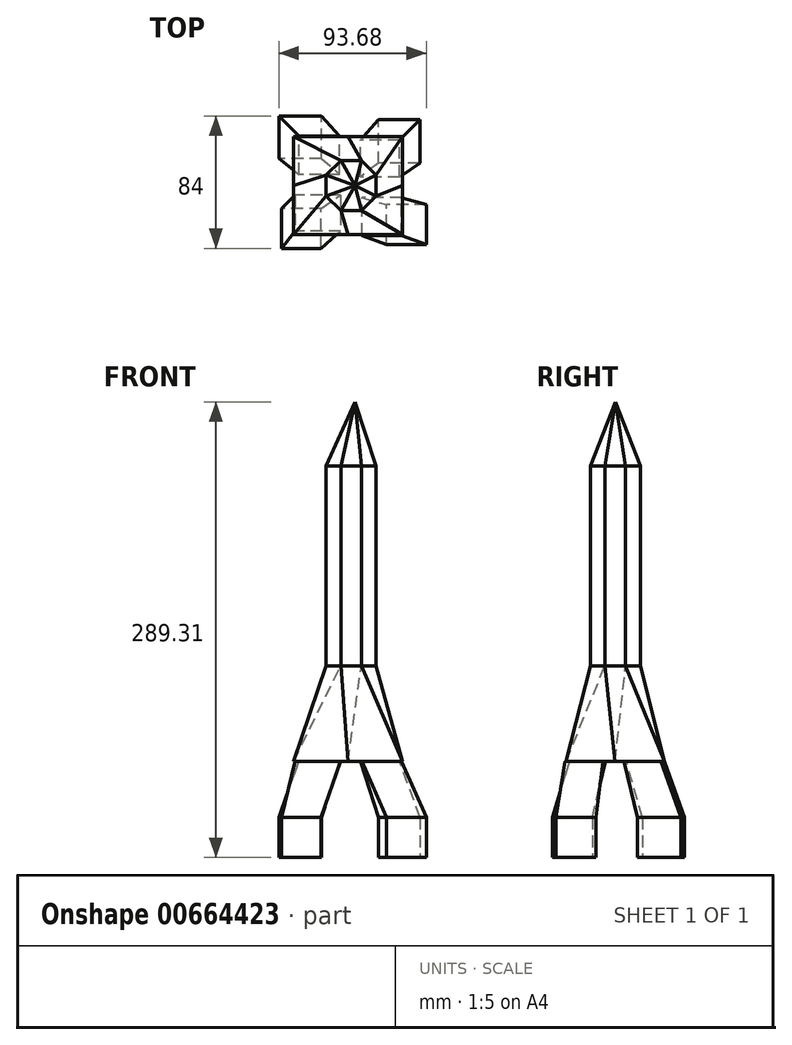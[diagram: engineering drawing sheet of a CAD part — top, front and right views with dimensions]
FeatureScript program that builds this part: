
annotation { "Feature Type Name" : "Feature", "Feature Type Description" : "" }
export const myFeature = defineFeature(function(context is Context, id is Id, definition is map)
    precondition{}
    {
        {
            var Q0;
            Q0=qCreatedBy(makeId("Top.planeOp"),FACE);
            var sketch = newSketch(context, id + "F0", { "sketchPlane" : qUnion([Q0])});
            skLineSegment(sketch, "E0.bottom", {"start": v(48.34, -37.68) * mm, "end": v(22.94, -37.68) * mm});
            skLineSegment(sketch, "E0.top", {"start": v(48.34, -12.28) * mm, "end": v(22.94, -12.28) * mm});
            skLineSegment(sketch, "E0.left", {"start": v(48.34, -37.68) * mm, "end": v(48.34, -12.28) * mm});
            skLineSegment(sketch, "E0.right", {"start": v(22.94, -37.68) * mm, "end": v(22.94, -12.28) * mm});
            skLineSegment(sketch, "E1.bottom", {"start": v(-18.47, -40.03) * mm, "end": v(-43.61, -40.03) * mm});
            skLineSegment(sketch, "E1.top", {"start": v(-18.47, -14.63) * mm, "end": v(-43.61, -14.63) * mm});
            skLineSegment(sketch, "E1.left", {"start": v(-18.47, -40.03) * mm, "end": v(-18.47, -14.63) * mm});
            skLineSegment(sketch, "E1.right", {"start": v(-43.61, -40.03) * mm, "end": v(-43.61, -14.63) * mm});
            skLineSegment(sketch, "E2.bottom", {"start": v(44.34, 14.1) * mm, "end": v(18.05, 14.1) * mm});
            skLineSegment(sketch, "E2.top", {"start": v(44.34, 41.53) * mm, "end": v(18.05, 41.53) * mm});
            skLineSegment(sketch, "E2.left", {"start": v(44.34, 14.1) * mm, "end": v(44.34, 41.53) * mm});
            skLineSegment(sketch, "E2.right", {"start": v(18.05, 14.1) * mm, "end": v(18.05, 41.53) * mm});
            skLineSegment(sketch, "E3.bottom", {"start": v(-18.32, 17.15) * mm, "end": v(-45.34, 17.15) * mm});
            skLineSegment(sketch, "E3.top", {"start": v(-18.32, 43.97) * mm, "end": v(-45.34, 43.97) * mm});
            skLineSegment(sketch, "E3.left", {"start": v(-18.32, 17.15) * mm, "end": v(-18.32, 43.97) * mm});
            skLineSegment(sketch, "E3.right", {"start": v(-45.34, 17.15) * mm, "end": v(-45.34, 43.97) * mm});
            skSolve(sketch);
        }
        {
            var Q0;
            Q0=makeQuery(id+"F0.imprint","IMPRINT",FACE,{"disambiguationData":[TD([[makeQuery(id+"F0.imprint","IMPRINT",EDGE,{"derivedFrom":sQuery(id+"F0.wireOp",EDGE,"E0.bottom")}),-1.0]])]});
            var Q1;
            Q1=makeQuery(id+"F0.imprint","IMPRINT",FACE,{"disambiguationData":[TD([[makeQuery(id+"F0.imprint","IMPRINT",EDGE,{"derivedFrom":sQuery(id+"F0.wireOp",EDGE,"E2.bottom")}),-1.0]])]});
            var Q2;
            Q2=makeQuery(id+"F0.imprint","IMPRINT",FACE,{"disambiguationData":[TD([[makeQuery(id+"F0.imprint","IMPRINT",EDGE,{"derivedFrom":sQuery(id+"F0.wireOp",EDGE,"E3.bottom")}),-1.0]])]});
            var Q3;
            Q3=makeQuery(id+"F0.imprint","IMPRINT",FACE,{"disambiguationData":[TD([[makeQuery(id+"F0.imprint","IMPRINT",EDGE,{"derivedFrom":sQuery(id+"F0.wireOp",EDGE,"E1.bottom")}),-1.0]])]});
            extrude(context, id + "F1", {"entities" : qUnion([Q0, Q1, Q2, Q3]), "depth" : 25.4 * mm, "offsetDistance" : 25.4 * mm});
        }
        {
            var Q0;
            Q0=makeQuery(id+"F1.opExtrude","CAP_FACE",FACE,{"disambiguationData":[OSD([sQuery(id+"F0.wireOp",EDGE,"E0.bottom"),sQuery(id+"F0.wireOp",EDGE,"E0.top"),sQuery(id+"F0.wireOp",EDGE,"E0.left"),sQuery(id+"F0.wireOp",EDGE,"E0.right")])],"isStart":false});
            cPlane(context, id + "F2", {"entities" : qUnion([Q0]), "cplaneType" : CPlaneType.OFFSET, "offset" : 35.56 * mm, "width" : 152.4 * mm, "height" : 152.4 * mm});
        }
        {
            var Q0;
            Q0=makeQuery(id+"F1.opExtrude","CAP_FACE",FACE,{"disambiguationData":[OSD([sQuery(id+"F0.wireOp",EDGE,"E3.bottom"),sQuery(id+"F0.wireOp",EDGE,"E3.top"),sQuery(id+"F0.wireOp",EDGE,"E3.left"),sQuery(id+"F0.wireOp",EDGE,"E3.right")])],"isStart":false});
            var sketch = newSketch(context, id + "F3", { "sketchPlane" : qUnion([Q0])});
            skSolve(sketch);
        }
        {
            var Q0;
            Q0=makeQuery(id+"F3.imprint","IMPRINT",FACE,{"disambiguationData":[TD([[makeQuery(id+"F3.imprint","IMPRINT",EDGE,{"derivedFrom":makeQuery(id+"F1.opExtrude","CAP_EDGE",EDGE,{"disambiguationData":[OSD([sQuery(id+"F0.wireOp",EDGE,"E3.bottom")])],"isStart":false})}),-1.0]])]});
            var sketch = newSketch(context, id + "F4", { "sketchPlane" : qUnion([Q0])});
            skLineSegment(sketch, "E4.bottom", {"start": v(-18.27, 43.99) * mm, "end": v(-45.5, 43.99) * mm});
            skLineSegment(sketch, "E4.top", {"start": v(-18.27, 17.13) * mm, "end": v(-45.5, 17.13) * mm});
            skLineSegment(sketch, "E4.left", {"start": v(-18.27, 43.99) * mm, "end": v(-18.27, 17.13) * mm});
            skLineSegment(sketch, "E4.right", {"start": v(-45.5, 43.99) * mm, "end": v(-45.5, 17.13) * mm});
            skLineSegment(sketch, "E5.bottom", {"start": v(44.38, 41.75) * mm, "end": v(18.04, 41.75) * mm});
            skLineSegment(sketch, "E5.top", {"start": v(44.38, 14.12) * mm, "end": v(18.04, 14.12) * mm});
            skLineSegment(sketch, "E5.left", {"start": v(44.38, 41.75) * mm, "end": v(44.38, 14.12) * mm});
            skLineSegment(sketch, "E5.right", {"start": v(18.04, 41.75) * mm, "end": v(18.04, 14.12) * mm});
            skLineSegment(sketch, "E6.bottom", {"start": v(48.26, -12.22) * mm, "end": v(22.94, -12.22) * mm});
            skLineSegment(sketch, "E6.top", {"start": v(48.26, -37.4) * mm, "end": v(22.94, -37.4) * mm});
            skLineSegment(sketch, "E6.left", {"start": v(48.26, -12.22) * mm, "end": v(48.26, -37.4) * mm});
            skLineSegment(sketch, "E6.right", {"start": v(22.94, -12.22) * mm, "end": v(22.94, -37.4) * mm});
            skLineSegment(sketch, "E7.bottom", {"start": v(-18.8, -14.52) * mm, "end": v(-43.7, -14.52) * mm});
            skLineSegment(sketch, "E7.top", {"start": v(-18.8, -39.99) * mm, "end": v(-43.7, -39.99) * mm});
            skLineSegment(sketch, "E7.left", {"start": v(-18.8, -14.52) * mm, "end": v(-18.8, -39.99) * mm});
            skLineSegment(sketch, "E7.right", {"start": v(-43.7, -14.52) * mm, "end": v(-43.7, -39.99) * mm});
            skSolve(sketch);
        }
        {
            var Q0;
            Q0=qCreatedBy(id+"F2.planeOp",FACE);
            var sketch = newSketch(context, id + "F5", { "sketchPlane" : qUnion([Q0])});
            skLineSegment(sketch, "E8.bottom", {"start": v(36.26, 35.18) * mm, "end": v(10.32, 35.18) * mm});
            skLineSegment(sketch, "E8.top", {"start": v(36.26, 8.93) * mm, "end": v(10.32, 8.93) * mm});
            skLineSegment(sketch, "E8.left", {"start": v(36.26, 35.18) * mm, "end": v(36.26, 8.93) * mm});
            skLineSegment(sketch, "E8.right", {"start": v(10.32, 35.18) * mm, "end": v(10.32, 8.93) * mm});
            skLineSegment(sketch, "E9.bottom", {"start": v(-6.68, 34.58) * mm, "end": v(-34.12, 34.58) * mm});
            skLineSegment(sketch, "E9.top", {"start": v(-6.68, 8.93) * mm, "end": v(-34.12, 8.93) * mm});
            skLineSegment(sketch, "E9.left", {"start": v(-6.68, 34.58) * mm, "end": v(-6.68, 8.93) * mm});
            skLineSegment(sketch, "E9.right", {"start": v(-34.12, 34.58) * mm, "end": v(-34.12, 8.93) * mm});
            skLineSegment(sketch, "E10.bottom", {"start": v(-6.09, -6.28) * mm, "end": v(-35.01, -6.28) * mm});
            skLineSegment(sketch, "E10.top", {"start": v(-6.09, -28.94) * mm, "end": v(-35.01, -28.94) * mm});
            skLineSegment(sketch, "E10.left", {"start": v(-6.09, -6.28) * mm, "end": v(-6.09, -28.94) * mm});
            skLineSegment(sketch, "E10.right", {"start": v(-35.01, -6.28) * mm, "end": v(-35.01, -28.94) * mm});
            skLineSegment(sketch, "E11.bottom", {"start": v(37.75, -5.38) * mm, "end": v(11.21, -5.38) * mm});
            skLineSegment(sketch, "E11.top", {"start": v(37.75, -28.94) * mm, "end": v(11.21, -28.94) * mm});
            skLineSegment(sketch, "E11.left", {"start": v(37.75, -5.38) * mm, "end": v(37.75, -28.94) * mm});
            skLineSegment(sketch, "E11.right", {"start": v(11.21, -5.38) * mm, "end": v(11.21, -28.94) * mm});
            skSolve(sketch);
        }
        {
            var Q1;
            Q1=makeQuery(id+"F1.opExtrude","CAP_FACE",FACE,{"disambiguationData":[OSD([sQuery(id+"F0.wireOp",EDGE,"E1.bottom"),sQuery(id+"F0.wireOp",EDGE,"E1.top"),sQuery(id+"F0.wireOp",EDGE,"E1.left"),sQuery(id+"F0.wireOp",EDGE,"E1.right")])],"isStart":false});
            var Q2;
            Q2=makeQuery(id+"F5.imprint","IMPRINT",FACE,{"disambiguationData":[TD([[makeQuery(id+"F5.imprint","IMPRINT",EDGE,{"derivedFrom":sQuery(id+"F5.wireOp",EDGE,"E10.bottom")}),1.0]])]});
            loft(context, id + "F6", {"operationType" : NewBodyOperationType.ADD, "sheetProfilesArray" : [{ "sheetProfileEntities" : qUnion([Q1]) }, { "sheetProfileEntities" : qUnion([Q2]) }]});
        }
        {
            var Q0;
            Q0=qCreatedBy(id+"F2.planeOp",FACE);
            var sketch = newSketch(context, id + "F7", { "sketchPlane" : qUnion([Q0])});
            skLineSegment(sketch, "E12.bottom", {"start": v(-8.35, 7.38) * mm, "end": v(-34.25, 7.38) * mm});
            skLineSegment(sketch, "E12.top", {"start": v(-8.35, 30.2) * mm, "end": v(-34.25, 30.2) * mm});
            skLineSegment(sketch, "E12.left", {"start": v(-8.35, 7.38) * mm, "end": v(-8.35, 30.2) * mm});
            skLineSegment(sketch, "E12.right", {"start": v(-34.25, 7.38) * mm, "end": v(-34.25, 30.2) * mm});
            skLineSegment(sketch, "E13.bottom", {"start": v(31.36, 5.4) * mm, "end": v(6.57, 5.4) * mm});
            skLineSegment(sketch, "E13.top", {"start": v(31.36, 28.89) * mm, "end": v(6.57, 28.89) * mm});
            skLineSegment(sketch, "E13.left", {"start": v(31.36, 5.4) * mm, "end": v(31.36, 28.89) * mm});
            skLineSegment(sketch, "E13.right", {"start": v(6.57, 5.4) * mm, "end": v(6.57, 28.89) * mm});
            skLineSegment(sketch, "E14.bottom", {"start": v(30.48, -29.48) * mm, "end": v(6.35, -29.48) * mm});
            skLineSegment(sketch, "E14.top", {"start": v(30.48, -7.32) * mm, "end": v(6.35, -7.32) * mm});
            skLineSegment(sketch, "E14.left", {"start": v(30.48, -29.48) * mm, "end": v(30.48, -7.32) * mm});
            skLineSegment(sketch, "E14.right", {"start": v(6.35, -29.48) * mm, "end": v(6.35, -7.32) * mm});
            skSolve(sketch);
        }
        {
            var Q1;
            Q1=makeQuery(id+"F4.imprint","IMPRINT",FACE,{"disambiguationData":[TD([[makeQuery(id+"F4.imprint","IMPRINT",EDGE,{"derivedFrom":sQuery(id+"F4.wireOp",EDGE,"E5.bottom")}),1.0]])]});
            var Q2;
            Q2=makeQuery(id+"F7.imprint","IMPRINT",FACE,{"disambiguationData":[TD([[makeQuery(id+"F7.imprint","IMPRINT",EDGE,{"derivedFrom":sQuery(id+"F7.wireOp",EDGE,"E13.bottom")}),-1.0]])]});
            loft(context, id + "F8", {"operationType" : NewBodyOperationType.ADD, "sheetProfilesArray" : [{ "sheetProfileEntities" : qUnion([Q1]) }, { "sheetProfileEntities" : qUnion([Q2]) }]});
        }
        {
            var Q0;
            Q0=qCreatedBy(id+"F2.planeOp",FACE);
            var sketch = newSketch(context, id + "F9", { "sketchPlane" : qUnion([Q0])});
            skLineSegment(sketch, "E15.bottom", {"start": v(32.64, -31.9) * mm, "end": v(7.33, -31.9) * mm});
            skLineSegment(sketch, "E15.top", {"start": v(32.64, -7.9) * mm, "end": v(7.33, -7.9) * mm});
            skLineSegment(sketch, "E15.left", {"start": v(32.64, -31.9) * mm, "end": v(32.64, -7.9) * mm});
            skLineSegment(sketch, "E15.right", {"start": v(7.33, -31.9) * mm, "end": v(7.33, -7.9) * mm});
            skSolve(sketch);
        }
        {
            var Q1;
            Q1=makeQuery(id+"F9.imprint","IMPRINT",FACE,{"disambiguationData":[TD([[makeQuery(id+"F9.imprint","IMPRINT",EDGE,{"derivedFrom":sQuery(id+"F9.wireOp",EDGE,"E15.bottom")}),-1.0]])]});
            var Q2;
            Q2=makeQuery(id+"F1.opExtrude","CAP_FACE",FACE,{"disambiguationData":[OSD([sQuery(id+"F0.wireOp",EDGE,"E0.bottom"),sQuery(id+"F0.wireOp",EDGE,"E0.top"),sQuery(id+"F0.wireOp",EDGE,"E0.left"),sQuery(id+"F0.wireOp",EDGE,"E0.right")])],"isStart":false});
            loft(context, id + "F10", {"operationType" : NewBodyOperationType.ADD, "sheetProfilesArray" : [{ "sheetProfileEntities" : qUnion([Q1]) }, { "sheetProfileEntities" : qUnion([Q2]) }]});
        }
        {
            var Q0;
            Q0=qCreatedBy(id+"F2.planeOp",FACE);
            var sketch = newSketch(context, id + "F11", { "sketchPlane" : qUnion([Q0])});
            skLineSegment(sketch, "E16.bottom", {"start": v(-6.76, 6.98) * mm, "end": v(-32.6, 6.98) * mm});
            skLineSegment(sketch, "E16.top", {"start": v(-6.76, 31.25) * mm, "end": v(-32.6, 31.25) * mm});
            skLineSegment(sketch, "E16.left", {"start": v(-6.76, 6.98) * mm, "end": v(-6.76, 31.25) * mm});
            skLineSegment(sketch, "E16.right", {"start": v(-32.6, 6.98) * mm, "end": v(-32.6, 31.25) * mm});
            skSolve(sketch);
        }
        {
            var Q1;
            Q1=makeQuery(id+"F3.imprint","IMPRINT",FACE,{"disambiguationData":[TD([[makeQuery(id+"F3.imprint","IMPRINT",EDGE,{"derivedFrom":makeQuery(id+"F1.opExtrude","CAP_EDGE",EDGE,{"disambiguationData":[OSD([sQuery(id+"F0.wireOp",EDGE,"E3.bottom")])],"isStart":false})}),-1.0]])]});
            var Q2;
            Q2=makeQuery(id+"F11.imprint","IMPRINT",FACE,{"disambiguationData":[TD([[makeQuery(id+"F11.imprint","IMPRINT",EDGE,{"derivedFrom":sQuery(id+"F11.wireOp",EDGE,"E16.bottom")}),-1.0]])]});
            loft(context, id + "F12", {"operationType" : NewBodyOperationType.ADD, "sheetProfilesArray" : [{ "sheetProfileEntities" : qUnion([Q1]) }, { "sheetProfileEntities" : qUnion([Q2]) }]});
        }
        {
            var Q0;
            Q0=qCreatedBy(id+"F2.planeOp",FACE);
            cPlane(context, id + "F13", {"entities" : qUnion([Q0]), "cplaneType" : CPlaneType.OFFSET, "offset" : 60.7 * mm, "width" : 152.4 * mm, "height" : 152.4 * mm});
        }
        {
            var Q0;
            Q0=qCreatedBy(id+"F13.planeOp",FACE);
            var sketch = newSketch(context, id + "F14", { "sketchPlane" : qUnion([Q0])});
            skCircle(sketch, "E17.cCircle", {"center": v(0.55, -0.07) * mm, "radius": 15.87 * mm, "construction": true});
            skLineSegment(sketch, "E17.0", {"start": v(-15.32, -6.65) * mm, "end": v(-15.32, 6.5) * mm});
            skLineSegment(sketch, "E17.1", {"start": v(-15.32, 6.5) * mm, "end": v(-6.02, 15.8) * mm});
            skLineSegment(sketch, "E17.2", {"start": v(-6.02, 15.8) * mm, "end": v(7.13, 15.8) * mm});
            skLineSegment(sketch, "E17.3", {"start": v(7.13, 15.8) * mm, "end": v(16.43, 6.5) * mm});
            skLineSegment(sketch, "E17.4", {"start": v(16.43, 6.5) * mm, "end": v(16.43, -6.65) * mm});
            skLineSegment(sketch, "E17.5", {"start": v(16.43, -6.65) * mm, "end": v(7.13, -15.95) * mm});
            skLineSegment(sketch, "E17.6", {"start": v(7.13, -15.95) * mm, "end": v(-6.02, -15.95) * mm});
            skLineSegment(sketch, "E17.7", {"start": v(-6.02, -15.95) * mm, "end": v(-15.32, -6.65) * mm});
            skPoint(sketch, "E17.0.midPoint", {"position": v(-15.32, -0.07) * mm});
            skSolve(sketch);
        }
        {
            var Q0;
            Q0=qCreatedBy(id+"F2.planeOp",FACE);
            var sketch = newSketch(context, id + "F15", { "sketchPlane" : qUnion([Q0])});
            skLineSegment(sketch, "E18.bottom", {"start": v(33.2, 31.03) * mm, "end": v(-35.96, 31.03) * mm});
            skLineSegment(sketch, "E18.top", {"start": v(33.2, -31.31) * mm, "end": v(-35.96, -31.31) * mm});
            skLineSegment(sketch, "E18.left", {"start": v(33.2, 31.03) * mm, "end": v(33.2, -31.31) * mm});
            skLineSegment(sketch, "E18.right", {"start": v(-35.96, 31.03) * mm, "end": v(-35.96, -31.31) * mm});
            skSolve(sketch);
        }
        {
            var Q0;
            Q0=makeQuery(id+"F15.imprint","IMPRINT",FACE,{"disambiguationData":[TD([[makeQuery(id+"F15.imprint","IMPRINT",EDGE,{"derivedFrom":sQuery(id+"F15.wireOp",EDGE,"E18.bottom")}),1.0]])]});
            var Q1;
            Q1=makeQuery(id+"F14.imprint","IMPRINT",FACE,{"disambiguationData":[TD([[makeQuery(id+"F14.imprint","IMPRINT",EDGE,{"derivedFrom":sQuery(id+"F14.wireOp",EDGE,"E17.0")}),-1.0]])]});
            loft(context, id + "F16", {"sheetProfilesArray" : [{ "sheetProfileEntities" : qUnion([Q0]) }, { "sheetProfileEntities" : qUnion([Q1]) }]});
        }
        {
            var Q0;
            Q0=makeQuery(id+"F14.imprint","IMPRINT",FACE,{"disambiguationData":[TD([[makeQuery(id+"F14.imprint","IMPRINT",EDGE,{"derivedFrom":sQuery(id+"F14.wireOp",EDGE,"E17.0")}),-1.0]])]});
            extrude(context, id + "F17", {"entities" : qUnion([Q0]), "operationType" : NewBodyOperationType.ADD, "depth" : 127 * mm, "offsetDistance" : 25.4 * mm});
        }
        {
            var Q0;
            Q0=makeQuery(id+"F17.opExtrude","CAP_FACE",FACE,{"disambiguationData":[OSD([sQuery(id+"F14.wireOp",EDGE,"E17.0"),sQuery(id+"F14.wireOp",EDGE,"E17.1"),sQuery(id+"F14.wireOp",EDGE,"E17.2"),sQuery(id+"F14.wireOp",EDGE,"E17.3"),sQuery(id+"F14.wireOp",EDGE,"E17.4"),sQuery(id+"F14.wireOp",EDGE,"E17.5"),sQuery(id+"F14.wireOp",EDGE,"E17.6"),sQuery(id+"F14.wireOp",EDGE,"E17.7")])],"isStart":false});
            var sketch = newSketch(context, id + "F18", { "sketchPlane" : qUnion([Q0])});
            skSolve(sketch);
        }
        {
            var Q0;
            Q0=makeQuery(id+"F18.imprint","IMPRINT",FACE,{"disambiguationData":[TD([[makeQuery(id+"F18.imprint","IMPRINT",EDGE,{"derivedFrom":makeQuery(id+"F17.opExtrude","CAP_EDGE",EDGE,{"disambiguationData":[OSD([sQuery(id+"F14.wireOp",EDGE,"E17.0")])],"isStart":false})}),-1.0]])]});
            cPlane(context, id + "F19", {"entities" : qUnion([Q0]), "cplaneType" : CPlaneType.OFFSET, "offset" : 40.64 * mm, "width" : 152.4 * mm, "height" : 152.4 * mm});
        }
        {
            var Q0;
            Q0=qCreatedBy(id+"F19.planeOp",FACE);
            var sketch = newSketch(context, id + "F20", { "sketchPlane" : qUnion([Q0])});
            skPoint(sketch, "E19", {"position": v(0, 0) * mm});
            skPoint(sketch, "E20", {"position": v(3.17, 0) * mm});
            skSolve(sketch);
        }
        {
            var Q1;
            Q1=sQuery(id+"F20.wireOp",VERTEX,"E20");
            var Q2;
            Q2=makeQuery(id+"F18.imprint","IMPRINT",FACE,{"disambiguationData":[TD([[makeQuery(id+"F18.imprint","IMPRINT",EDGE,{"derivedFrom":makeQuery(id+"F17.opExtrude","CAP_EDGE",EDGE,{"disambiguationData":[OSD([sQuery(id+"F14.wireOp",EDGE,"E17.0")])],"isStart":false})}),-1.0]])]});
            loft(context, id + "F21", {"operationType" : NewBodyOperationType.ADD, "sheetProfilesArray" : [{ "sheetProfileEntities" : qUnion([Q1]) }, { "sheetProfileEntities" : qUnion([Q2]) }]});
        }
    });
